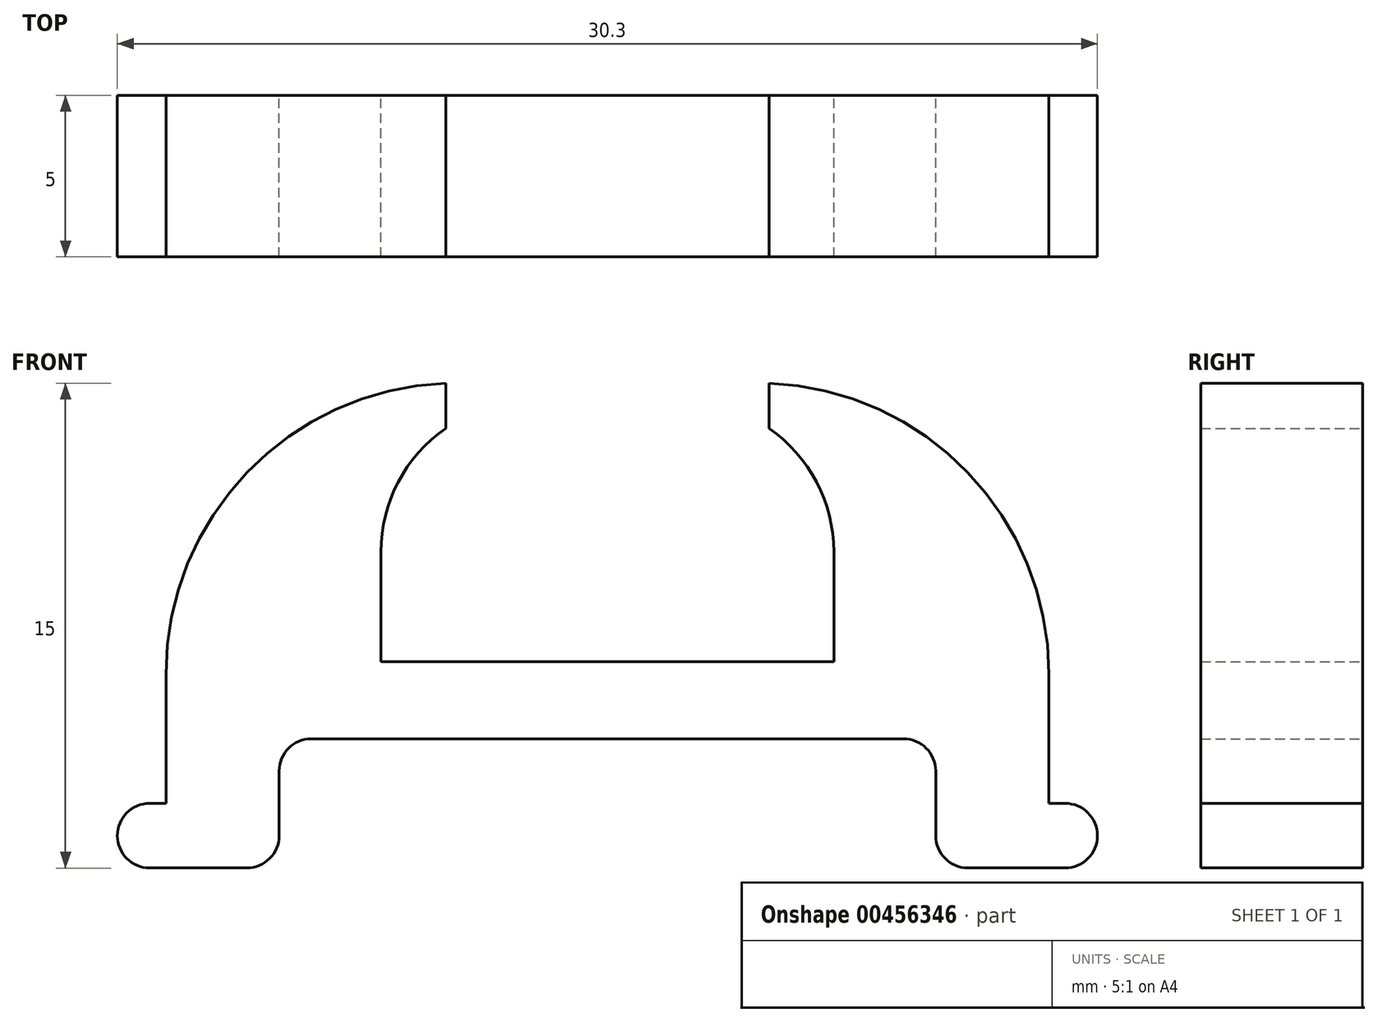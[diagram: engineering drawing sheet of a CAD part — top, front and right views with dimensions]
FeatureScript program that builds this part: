
annotation { "Feature Type Name" : "Feature", "Feature Type Description" : "" }
export const myFeature = defineFeature(function(context is Context, id is Id, definition is map)
    precondition{}
    {
        {
            var Q0;
            Q0=qCreatedBy(makeId("Front.planeOp"),FACE);
            var sketch = newSketch(context, id + "F0", { "sketchPlane" : qUnion([Q0])});
            skLineSegment(sketch, "E0", {"start": v(0, -4.74) * mm, "end": v(-7, -4.74) * mm});
            skLineSegment(sketch, "E1", {"start": v(-7, -4.74) * mm, "end": v(-7, -1.34) * mm});
            skPoint(sketch, "E2.visualSharp", {"position": v(-7, 3.95) * mm});
            skArc(sketch, "E2.filletArc", {"start": v(-5, 2.48) * mm, "mid": v(-6.47, 0.82) * mm, "end": v(-7, -1.34) * mm});
            skLineSegment(sketch, "E3", {"start": v(-5, 3.88) * mm, "end": v(-5, 2.48) * mm});
            skPoint(sketch, "E4", {"position": v(2, -5.12) * mm});
            skPoint(sketch, "E5", {"position": v(-5, 2.6) * mm});
            skPoint(sketch, "E6", {"position": v(0, 3.88) * mm});
            skPoint(sketch, "E7", {"position": v(0, -4.74) * mm});
            skPoint(sketch, "E8", {"position": v(-5, 2.48) * mm});
            skLineSegment(sketch, "E9", {"start": v(0, 3.88) * mm, "end": v(0, -5.12) * mm});
            skPoint(sketch, "E10.orphan", {"position": v(-4.73, 2.66) * mm});
            skLineSegment(sketch, "E11", {"start": v(-5, 3.88) * mm, "end": v(0, 3.88) * mm});
            skPoint(sketch, "E12", {"position": v(0, -5.12) * mm});
            skSolve(sketch);
        }
        {
            var Q0;
            Q0=qCreatedBy(makeId("Front.planeOp"),FACE);
            var sketch = newSketch(context, id + "F1", { "sketchPlane" : qUnion([Q0])});
            skLineSegment(sketch, "E13", {"start": v(-14.15, -9.12) * mm, "end": v(-13.65, -9.12) * mm});
            skLineSegment(sketch, "E14", {"start": v(-13.65, -9.12) * mm, "end": v(-13.65, -5.12) * mm});
            skLineSegment(sketch, "E15", {"start": v(-15.15, -10.12) * mm, "end": v(-15.15, -10.12) * mm});
            skLineSegment(sketch, "E16", {"start": v(-14.15, -11.12) * mm, "end": v(-11.15, -11.12) * mm});
            skLineSegment(sketch, "E17", {"start": v(-10.15, -10.12) * mm, "end": v(-10.15, -8.12) * mm});
            skLineSegment(sketch, "E18", {"start": v(-9.15, -7.12) * mm, "end": v(0, -7.12) * mm});
            skLineSegment(sketch, "E19", {"start": v(0, -7.12) * mm, "end": v(0, -4.74) * mm});
            skPoint(sketch, "E20.visualSharp", {"position": v(-15.15, -9.12) * mm});
            skArc(sketch, "E20.filletArc", {"start": v(-14.15, -9.12) * mm, "mid": v(-14.86, -9.41) * mm, "end": v(-15.15, -10.12) * mm});
            skPoint(sketch, "E21.visualSharp", {"position": v(-15.15, -11.12) * mm});
            skArc(sketch, "E21.filletArc", {"start": v(-15.15, -10.12) * mm, "mid": v(-14.86, -10.83) * mm, "end": v(-14.15, -11.12) * mm});
            skPoint(sketch, "E22.visualSharp", {"position": v(-10.15, -11.12) * mm});
            skArc(sketch, "E22.filletArc", {"start": v(-11.15, -11.12) * mm, "mid": v(-10.44, -10.83) * mm, "end": v(-10.15, -10.12) * mm});
            skPoint(sketch, "E23.visualSharp", {"position": v(-10.15, -7.12) * mm});
            skArc(sketch, "E23.filletArc", {"start": v(-9.15, -7.12) * mm, "mid": v(-9.86, -7.41) * mm, "end": v(-10.15, -8.12) * mm});
            skPoint(sketch, "E24.visualSharp", {"position": v(-13.65, 3.88) * mm});
            skArc(sketch, "E24.filletArc", {"start": v(-5, 3.88) * mm, "mid": v(-11.14, 1.12) * mm, "end": v(-13.65, -5.12) * mm});
            skPoint(sketch, "E25", {"position": v(0, -5.12) * mm});
            skLineSegment(sketch, "E26.0.2", {"start": v(-5, 3.88) * mm, "end": v(-5, 2.48) * mm});
            skArc(sketch, "E26.0.3", {"start": v(-5, 2.48) * mm, "mid": v(-6.47, 0.82) * mm, "end": v(-7, -1.34) * mm});
            skLineSegment(sketch, "E26.0.4", {"start": v(-7, -1.34) * mm, "end": v(-7, -4.74) * mm});
            skLineSegment(sketch, "E26.0.5", {"start": v(-7, -4.74) * mm, "end": v(0, -4.74) * mm});
            skPoint(sketch, "E26.0.0.end.orphan", {"position": v(0, 3.88) * mm});
            skSolve(sketch);
        }
        {
            var Q0;
            Q0=makeQuery(id+"F1.imprint","IMPRINT",FACE,{"disambiguationData":[TD([[makeQuery(id+"F1.imprint","IMPRINT",EDGE,{"derivedFrom":sQuery(id+"F1.wireOp",EDGE,"E13")}),-1.0]])]});
            extrude(context, id + "F2", {"entities" : qUnion([Q0]), "endBound" : BoundingType.SYMMETRIC, "depth" : 5 * mm});
        }
        {
            var Q0;
            Q0=makeQuery(id+"F2.opExtrude","SWEPT_BODY",BODY,{"disambiguationData":[OSD([sQuery(id+"F1.wireOp",EDGE,"E13"),sQuery(id+"F1.wireOp",EDGE,"E14"),sQuery(id+"F1.wireOp",EDGE,"E16"),sQuery(id+"F1.wireOp",EDGE,"E17"),sQuery(id+"F1.wireOp",EDGE,"E18"),sQuery(id+"F1.wireOp",EDGE,"E19"),sQuery(id+"F1.wireOp",EDGE,"E20.filletArc"),sQuery(id+"F1.wireOp",EDGE,"E21.filletArc"),sQuery(id+"F1.wireOp",EDGE,"E22.filletArc"),sQuery(id+"F1.wireOp",EDGE,"E23.filletArc"),sQuery(id+"F1.wireOp",EDGE,"E24.filletArc"),sQuery(id+"F1.wireOp",EDGE,"E26.0.2"),sQuery(id+"F1.wireOp",EDGE,"E26.0.3"),sQuery(id+"F1.wireOp",EDGE,"E26.0.4"),sQuery(id+"F1.wireOp",EDGE,"E26.0.5")])]});
            var Q1;
            Q1=makeQuery(id+"F2.opExtrude","SWEPT_FACE",FACE,{"disambiguationData":[OSD([sQuery(id+"F1.wireOp",EDGE,"E19")])]});
            mirror(context, id + "F3", {"operationType" : NewBodyOperationType.ADD, "entities" : qUnion([Q0]), "mirrorPlane" : qUnion([Q1])});
        }
    });
